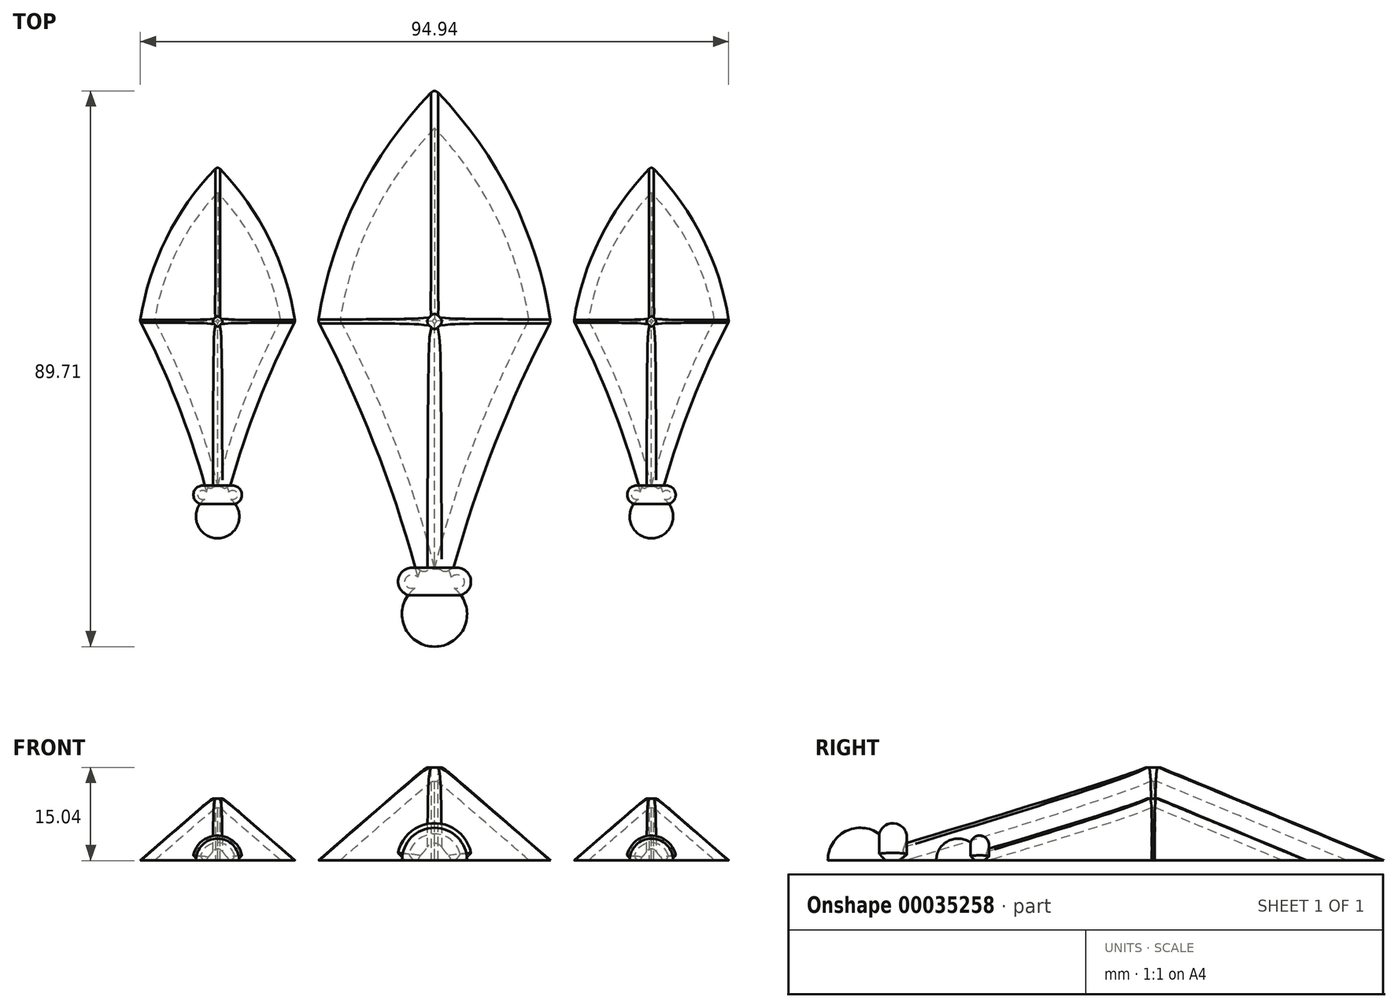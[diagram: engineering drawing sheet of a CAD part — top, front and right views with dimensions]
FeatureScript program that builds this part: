
annotation { "Feature Type Name" : "Feature", "Feature Type Description" : "" }
export const myFeature = defineFeature(function(context is Context, id is Id, definition is map)
    precondition{}
    {
        {
            var Q0;
            Q0=qCreatedBy(makeId("Top.planeOp"),FACE);
            var sketch = newSketch(context, id + "F0", { "sketchPlane" : qUnion([Q0])});
            skLineSegment(sketch, "E0", {"start": v(0, 0) * mm, "end": v(0, 25) * mm, "construction": true});
            skLineSegment(sketch, "E1", {"start": v(-12.5, 0) * mm, "end": v(12.5, 0) * mm, "construction": true});
            skLineSegment(sketch, "E2", {"start": v(0, 0) * mm, "end": v(0, -25) * mm, "construction": true});
            skLineSegment(sketch, "E3", {"start": v(0, -25) * mm, "end": v(0, -35) * mm, "construction": true});
            skArc(sketch, "E4", {"start": v(0, 25) * mm, "mid": v(-8.24, 13.5) * mm, "end": v(-12.5, 0) * mm});
            skArc(sketch, "E5", {"start": v(0, -35) * mm, "mid": v(-5.04, -17.07) * mm, "end": v(-12.5, 0) * mm});
            skArc(sketch, "E6.MirrorCS", {"start": v(0, 25) * mm, "mid": v(8.24, 13.5) * mm, "end": v(12.5, 0) * mm});
            skArc(sketch, "E7.MirrorCS", {"start": v(0, -35) * mm, "mid": v(5.04, -17.07) * mm, "end": v(12.5, 0) * mm});
            skSolve(sketch);
        }
        {
            var Q0;
            Q0=makeQuery(id+"F0.imprint","IMPRINT",FACE,{"disambiguationData":[TD([[makeQuery(id+"F0.imprint","IMPRINT",EDGE,{"derivedFrom":sQuery(id+"F0.wireOp",EDGE,"E4")}),1.0]])]});
            cPlane(context, id + "F1", {"entities" : qUnion([Q0]), "cplaneType" : CPlaneType.OFFSET, "offset" : 10 * mm, "width" : 150 * mm, "height" : 150 * mm});
        }
        {
            var Q0;
            Q0=qCreatedBy(id+"F1.planeOp",FACE);
            var sketch = newSketch(context, id + "F2", { "sketchPlane" : qUnion([Q0])});
            skLineSegment(sketch, "E8", {"start": v(-1, 0) * mm, "end": v(1, 0) * mm, "construction": true});
            skLineSegment(sketch, "E9", {"start": v(0, 1) * mm, "end": v(0, -1) * mm, "construction": true});
            skLineSegment(sketch, "E10", {"start": v(0, 1) * mm, "end": v(-1, 0) * mm});
            skLineSegment(sketch, "E11", {"start": v(-1, 0) * mm, "end": v(0, -1) * mm});
            skLineSegment(sketch, "E12", {"start": v(0, -1) * mm, "end": v(1, 0) * mm});
            skLineSegment(sketch, "E13", {"start": v(1, 0) * mm, "end": v(0, 1) * mm});
            skSolve(sketch);
        }
        {
            var Q0;
            Q0=makeQuery(id+"F0.imprint","IMPRINT",FACE,{"disambiguationData":[TD([[makeQuery(id+"F0.imprint","IMPRINT",EDGE,{"derivedFrom":sQuery(id+"F0.wireOp",EDGE,"E4")}),1.0]])]});
            var Q1;
            Q1=makeQuery(id+"F2.imprint","IMPRINT",FACE,{"disambiguationData":[TD([[makeQuery(id+"F2.imprint","IMPRINT",EDGE,{"derivedFrom":sQuery(id+"F2.wireOp",EDGE,"E10")}),1.0]])]});
            loft(context, id + "F3", {"sheetProfilesArray" : [{ "sheetProfileEntities" : qUnion([Q0]) }, { "sheetProfileEntities" : qUnion([Q1]) }]});
        }
        {
            var Q0;
            Q0=qCreatedBy(makeId("Top.planeOp"),FACE);
            var sketch = newSketch(context, id + "F4", { "sketchPlane" : qUnion([Q0])});
            skPoint(sketch, "E14.0", {"position": v(0, -35) * mm});
            skLineSegment(sketch, "E15", {"start": v(-2.5, -28) * mm, "end": v(2.5, -28) * mm, "construction": true});
            skCircle(sketch, "E16", {"center": v(2.5, -28) * mm, "radius": 1.5 * mm});
            skLineSegment(sketch, "E17", {"start": v(0, -28) * mm, "end": v(0, -35) * mm});
            skArc(sketch, "E18", {"start": v(0, -35) * mm, "mid": v(3.5, -31.5) * mm, "end": v(0, -28) * mm});
            skSolve(sketch);
        }
        {
            var Q0;
            Q0 = qSketchRegion(id + "F4", true);
            var Q1;
            Q1=sQuery(id+"F4.wireOp",EDGE,"E17");
            revolve(context, id + "F5", {"operationType" : NewBodyOperationType.ADD, "entities" : qUnion([Q0]), "axis" : qUnion([Q1]), "revolveType" : RevolveType.ONE_DIRECTION, "angle" : 180 * degree});
        }
        {
            var Q0;
            Q0=makeQuery(id+"F5.boolean.opBoolean","MERGE",FACE,{"derivedFrom":[makeQuery(id+"F3.opLoft","CAP_FACE",FACE,{"disambiguationData":[OSD([makeQuery(id+"F0.imprint","IMPRINT",FACE,{"disambiguationData":[TD([[makeQuery(id+"F0.imprint","IMPRINT",EDGE,{"derivedFrom":sQuery(id+"F0.wireOp",EDGE,"E4")}),1.0]])]})])],"isStart":true}),makeQuery(id+"F5.opRevolve","CAP_FACE",FACE,{"disambiguationData":[OSD([sQuery(id+"F4.wireOp",EDGE,"E16"),sQuery(id+"F4.wireOp",EDGE,"E17"),sQuery(id+"F4.wireOp",EDGE,"E18")])],"isStart":true})]});
            shell(context, id + "F6", {"entities" : qUnion([Q0]), "thickness" : 1.5 * mm});
        }
        {
            var Q0;
            Q0=makeQuery(id+"F3.opLoft","SWEPT_EDGE",EDGE,{"disambiguationData":[OSD([sQuery(id+"F0.wireOp",EDGE,"E4"),sQuery(id+"F0.wireOp",EDGE,"E6.MirrorCS"),sQuery(id+"F2.wireOp",EDGE,"E10"),sQuery(id+"F2.wireOp",EDGE,"E13")])]});
            var Q1;
            Q1=makeQuery(id+"F3.opLoft","SWEPT_EDGE",EDGE,{"disambiguationData":[OSD([sQuery(id+"F0.wireOp",EDGE,"E4"),sQuery(id+"F0.wireOp",EDGE,"E5"),sQuery(id+"F2.wireOp",EDGE,"E10"),sQuery(id+"F2.wireOp",EDGE,"E11")])]});
            var Q2;
            Q2=makeQuery(id+"F3.opLoft","SWEPT_EDGE",EDGE,{"disambiguationData":[OSD([sQuery(id+"F0.wireOp",EDGE,"E6.MirrorCS"),sQuery(id+"F0.wireOp",EDGE,"E7.MirrorCS"),sQuery(id+"F2.wireOp",EDGE,"E12"),sQuery(id+"F2.wireOp",EDGE,"E13")])]});
            var Q3;
            Q3=makeQuery(id+"F3.opLoft","SWEPT_EDGE",EDGE,{"disambiguationData":[OSD([sQuery(id+"F0.wireOp",EDGE,"E5"),sQuery(id+"F0.wireOp",EDGE,"E7.MirrorCS"),sQuery(id+"F2.wireOp",EDGE,"E11"),sQuery(id+"F2.wireOp",EDGE,"E12")])]});
            var Q4;
            Q4=makeQuery(id+"F3.opLoft","CAP_FACE",FACE,{"disambiguationData":[OSD([makeQuery(id+"F2.imprint","IMPRINT",FACE,{"disambiguationData":[TD([[makeQuery(id+"F2.imprint","IMPRINT",EDGE,{"derivedFrom":sQuery(id+"F2.wireOp",EDGE,"E10")}),1.0]])]})])],"isStart":true});
            fillet(context, id + "F7", {"entities" : qUnion([Q0, Q1, Q2, Q3, Q4]), "radius" : 1 * mm, "tangentPropagation" : true, "allowEdgeOverflow" : false});
        }
        {
            var Q0;
            Q0=makeQuery(id+"F3.opLoft","MID_CAP_EDGE",EDGE,{"disambiguationData":[OSD([sQuery(id+"F0.wireOp",EDGE,"E4"),sQuery(id+"F0.wireOp",EDGE,"E5"),sQuery(id+"F0.wireOp",EDGE,"E6.MirrorCS")])],"capPos":0.0});
            var Q1;
            Q1=makeQuery(id+"F5.opRevolve","CAP_EDGE",EDGE,{"disambiguationData":[OSD([sQuery(id+"F4.wireOp",EDGE,"E16")])],"isStart":false});
            var Q2;
            Q2=makeQuery(id+"F5.opRevolve","CAP_EDGE",EDGE,{"disambiguationData":[OSD([sQuery(id+"F4.wireOp",EDGE,"E16")])],"isStart":true});
            var Q3;
            {var subQ0=sQuery(id+"F4.wireOp",EDGE,"E18");Q3=makeQuery(id+"F5.opRevolve","CAP_EDGE",EDGE,{"disambiguationData":[OSD([subQ0]),TDD([makeQuery(id+"F4.imprint","IMPRINT",EDGE,{"disambiguationData":[TD([[makeQuery(id+"F4.imprint","INTERSECT",VERTEX,{"disambiguationData":[OD(1.0)],"derivedFrom":[sQuery(id+"F4.wireOp",EDGE,"E17"),subQ0]}),-1.0]])],"derivedFrom":subQ0})])],"isStart":true});}
            chamfer(context, id + "F8", {"entities" : qUnion([Q0, Q1, Q2, Q3]), "width" : .8 * mm, "tangentPropagation" : true});
        }
        {
            var Q0;
            Q0=makeQuery(id+"F3.opLoft","SWEPT_BODY",BODY,{"disambiguationData":[OSD([makeQuery(id+"F0.imprint","IMPRINT",FACE,{"disambiguationData":[TD([[makeQuery(id+"F0.imprint","IMPRINT",EDGE,{"derivedFrom":sQuery(id+"F0.wireOp",EDGE,"E4")}),1.0]])]}),makeQuery(id+"F2.imprint","IMPRINT",FACE,{"disambiguationData":[TD([[makeQuery(id+"F2.imprint","IMPRINT",EDGE,{"derivedFrom":sQuery(id+"F2.wireOp",EDGE,"E10")}),1.0]])]})])]});
            transform(context, id + "F9", {"entities" : qUnion([Q0]), "transformType" : TransformType.TRANSLATION_3D, "dx" : 35 * mm, "dy" : 0 * mm, "dz" : 0 * mm, "makeCopy" : true});
        }
        {
            var Q0;
            Q0=makeQuery(id+"F3.opLoft","SWEPT_BODY",BODY,{"disambiguationData":[OSD([makeQuery(id+"F0.imprint","IMPRINT",FACE,{"disambiguationData":[TD([[makeQuery(id+"F0.imprint","IMPRINT",EDGE,{"derivedFrom":sQuery(id+"F0.wireOp",EDGE,"E4")}),1.0]])]}),makeQuery(id+"F2.imprint","IMPRINT",FACE,{"disambiguationData":[TD([[makeQuery(id+"F2.imprint","IMPRINT",EDGE,{"derivedFrom":sQuery(id+"F2.wireOp",EDGE,"E10")}),1.0]])]})])]});
            transform(context, id + "F10", {"entities" : qUnion([Q0]), "transformType" : TransformType.TRANSLATION_3D, "dx" : -35 * mm, "dy" : 0 * mm, "dz" : 0 * mm, "makeCopy" : true});
        }
        {
            var Q0;
            Q0=makeQuery(id+"F3.opLoft","SWEPT_BODY",BODY,{"disambiguationData":[OSD([makeQuery(id+"F0.imprint","IMPRINT",FACE,{"disambiguationData":[TD([[makeQuery(id+"F0.imprint","IMPRINT",EDGE,{"derivedFrom":sQuery(id+"F0.wireOp",EDGE,"E4")}),1.0]])]}),makeQuery(id+"F2.imprint","IMPRINT",FACE,{"disambiguationData":[TD([[makeQuery(id+"F2.imprint","IMPRINT",EDGE,{"derivedFrom":sQuery(id+"F2.wireOp",EDGE,"E10")}),1.0]])]})])]});
            var Q1;
            Q1=sQuery(id+"F0.wireOp",VERTEX,"E2.start");
            transform(context, id + "F11", {"entities" : qUnion([Q0]), "transformType" : TransformType.SCALE_UNIFORMLY, "scale" : 1.5, "makeCopy" : false, "scalePoint" : qUnion([Q1])});
        }
    });
